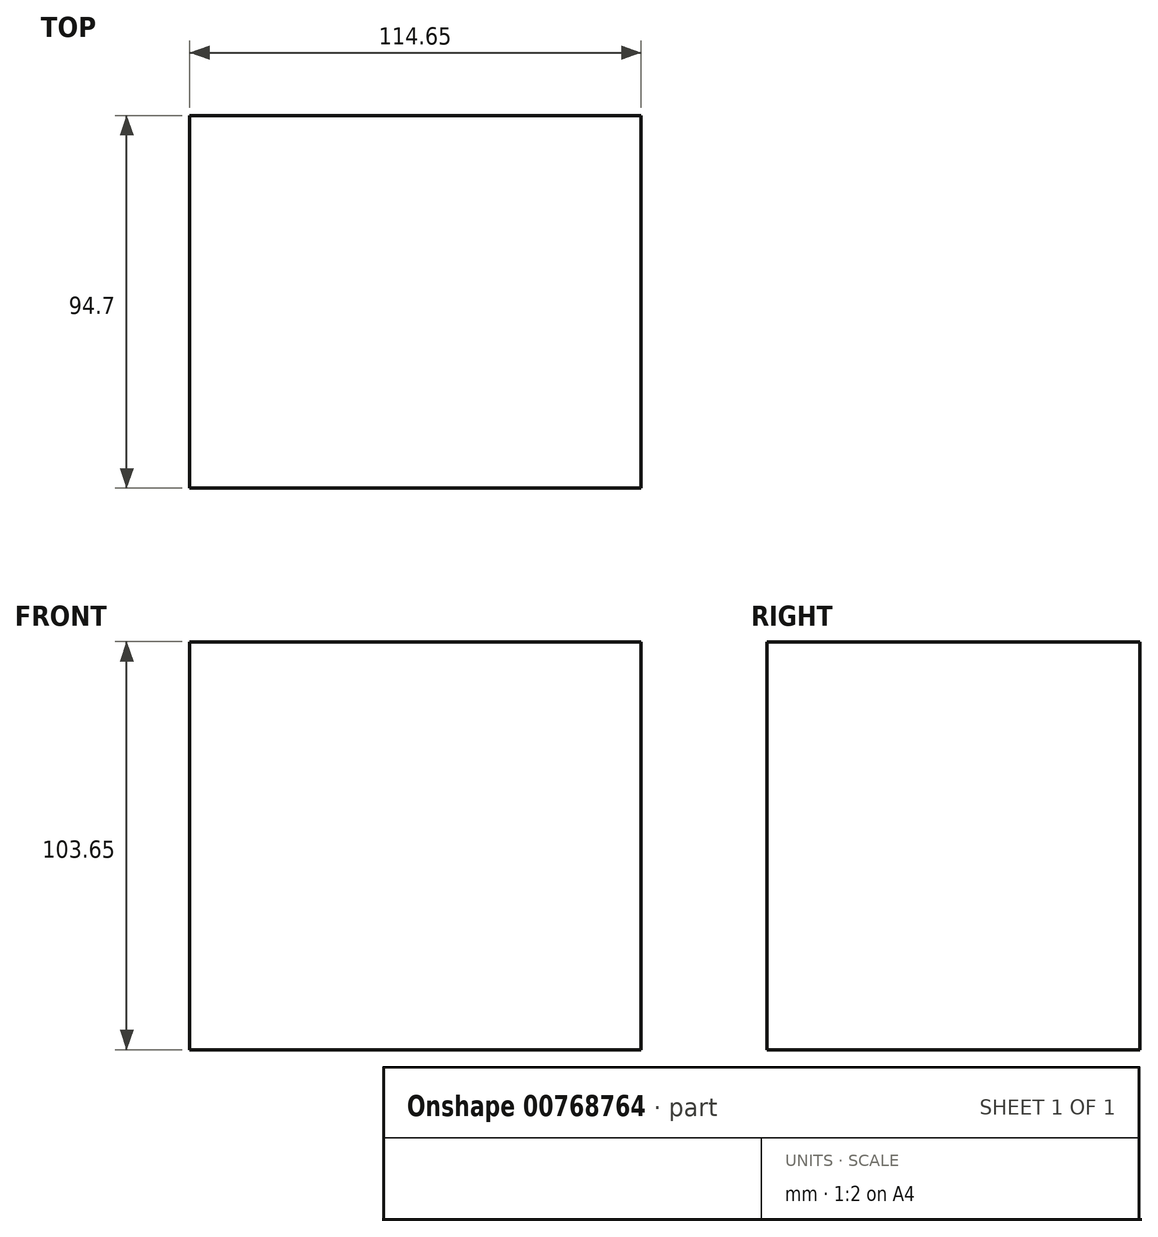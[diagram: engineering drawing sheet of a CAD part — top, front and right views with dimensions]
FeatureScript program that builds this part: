
annotation { "Feature Type Name" : "Feature", "Feature Type Description" : "" }
export const myFeature = defineFeature(function(context is Context, id is Id, definition is map)
    precondition{}
    {
        {
            var Q0;
            Q0=qCreatedBy(makeId("Front.planeOp"),FACE);
            var sketch = newSketch(context, id + "F0", { "sketchPlane" : qUnion([Q0])});
            skLineSegment(sketch, "E0.bottom", {"start": v(43.46, -14.1) * mm, "end": v(-71.2, -14.1) * mm});
            skLineSegment(sketch, "E0.top", {"start": v(43.46, 89.55) * mm, "end": v(-71.2, 89.55) * mm});
            skLineSegment(sketch, "E0.left", {"start": v(43.46, -14.1) * mm, "end": v(43.46, 89.55) * mm});
            skLineSegment(sketch, "E0.right", {"start": v(-71.2, -14.1) * mm, "end": v(-71.2, 89.55) * mm});
            skSolve(sketch);
        }
        {
            var Q0;
            Q0 = qSketchRegion(id + "F0", true);
            extrude(context, id + "F1", {"entities" : qUnion([Q0]), "oppositeDirection" : true, "depth" : 94.7 * mm, "offsetDistance" : 25.4 * mm});
        }
    });
